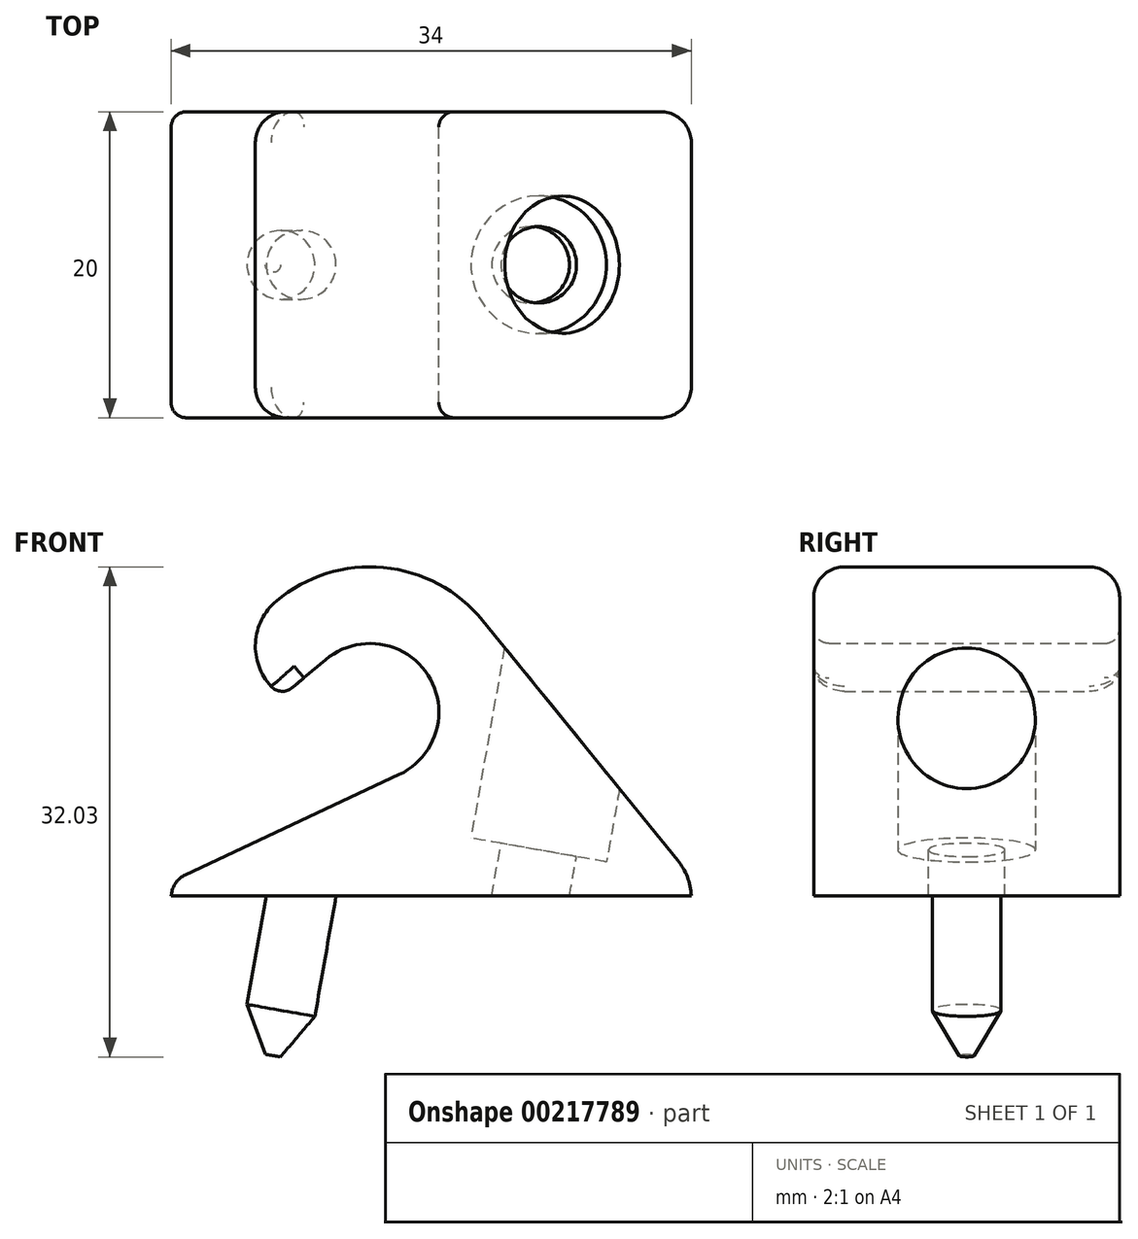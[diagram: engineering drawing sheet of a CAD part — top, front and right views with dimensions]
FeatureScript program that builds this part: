
annotation { "Feature Type Name" : "Feature", "Feature Type Description" : "" }
export const myFeature = defineFeature(function(context is Context, id is Id, definition is map)
    precondition{}
    {
        {
            var Q0;
            Q0=qCreatedBy(makeId("Front.planeOp"),FACE);
            var sketch = newSketch(context, id + "F0", { "sketchPlane" : qUnion([Q0])});
            skLineSegment(sketch, "E0", {"start": v(0, 0) * mm, "end": v(37, 0) * mm});
            skLineSegment(sketch, "E1", {"start": v(35.1, 2.33) * mm, "end": v(22.37, 18) * mm});
            skArc(sketch, "E2", {"start": v(16.9, 7.93) * mm, "mid": v(18.8, 14.43) * mm, "end": v(12.1, 15.44) * mm});
            skLineSegment(sketch, "E3", {"start": v(16.9, 7.93) * mm, "end": v(2.93, 1.37) * mm});
            skArc(sketch, "E4", {"start": v(22.37, 18) * mm, "mid": v(15.9, 21.46) * mm, "end": v(8.88, 19.27) * mm});
            skLineSegment(sketch, "E5", {"start": v(12.1, 15.44) * mm, "end": v(9.92, 13.6) * mm});
            skLineSegment(sketch, "E6", {"start": v(8.28, 14.37) * mm, "end": v(8.28, 14.37) * mm});
            skPoint(sketch, "E7.newPointB", {"position": v(8.28, 12.22) * mm});
            skArc(sketch, "E7.filletArc", {"start": v(8.28, 14.37) * mm, "mid": v(8.86, 13.46) * mm, "end": v(9.92, 13.6) * mm});
            skLineSegment(sketch, "E8", {"start": v(2, 0) * mm, "end": v(2.04, 0.2) * mm});
            skPoint(sketch, "E9.newPointB", {"position": v(0, 0) * mm});
            skArc(sketch, "E9.filletArc", {"start": v(2.93, 1.37) * mm, "mid": v(2.34, 0.9) * mm, "end": v(2.04, 0.2) * mm});
            skPoint(sketch, "E10.newPointA", {"position": v(37, 0) * mm});
            skArc(sketch, "E10.filletArc", {"start": v(36, 0) * mm, "mid": v(35.74, 1.23) * mm, "end": v(35.1, 2.33) * mm});
            skLineSegment(sketch, "E11", {"start": v(15, 12) * mm, "end": v(9.07, 19.04) * mm, "construction": true});
            skArc(sketch, "E12", {"start": v(8.88, 19.27) * mm, "mid": v(7.52, 16.55) * mm, "end": v(8.55, 13.69) * mm});
            skLineSegment(sketch, "E13", {"start": v(-3.54, 8.21) * mm, "end": v(45.39, -0.41) * mm, "construction": true});
            skPoint(sketch, "E14", {"position": v(26.03, 3) * mm});
            skLineSegment(sketch, "E15", {"start": v(26.03, 3) * mm, "end": v(24.94, -3.2) * mm, "construction": true});
            skPoint(sketch, "E16", {"position": v(25.5, 0) * mm});
            skLineSegment(sketch, "E17", {"start": v(11.48, 5.57) * mm, "end": v(10.5, 0) * mm, "construction": true});
            skLineSegment(sketch, "E18.0", {"start": v(-4.45, 3.04) * mm, "end": v(44.48, -5.59) * mm, "construction": true});
            skPoint(sketch, "E19", {"position": v(10.57, 0.4) * mm});
            skPoint(sketch, "E20", {"position": v(12.78, 0) * mm});
            skPoint(sketch, "E21.start.orphan", {"position": v(36, 0) * mm});
            skSolve(sketch);
        }
        {
            var Q0;
            Q0 = qSketchRegion(id + "F0", true);
            extrude(context, id + "F1", {"entities" : qUnion([Q0]), "endBound" : BoundingType.SYMMETRIC, "depth" : 20 * mm});
        }
        {
            var Q0;
            Q0=sQuery(id+"F0.wireOp",EDGE,"E13");
            cPlane(context, id + "F2", {"entities" : qUnion([Q0]), "cplaneType" : CPlaneType.LINE_ANGLE, "offset" : 25 * mm, "angle" : 90 * degree, "width" : 150 * mm, "height" : 150 * mm});
        }
        {
            var Q0;
            Q0=qCreatedBy(id+"F2.planeOp",FACE);
            var sketch = newSketch(context, id + "F3", { "sketchPlane" : qUnion([Q0])});
            skCircle(sketch, "E22", {"center": v(25.11, 0) * mm, "radius": 4.5 * mm});
            skSolve(sketch);
        }
        {
            var Q0;
            Q0 = qSketchRegion(id + "F3", true);
            extrude(context, id + "F4", {"entities" : qUnion([Q0]), "operationType" : NewBodyOperationType.REMOVE, "endBound" : BoundingType.THROUGH_ALL, "depth" : 25 * mm});
        }
        {
            var Q0;
            Q0=qCreatedBy(id+"F2.planeOp",FACE);
            var sketch = newSketch(context, id + "F5", { "sketchPlane" : qUnion([Q0])});
            skCircle(sketch, "E23", {"center": v(25.11, 0) * mm, "radius": 2.5 * mm});
            skSolve(sketch);
        }
        {
            var Q0;
            Q0 = qSketchRegion(id + "F5", true);
            extrude(context, id + "F6", {"entities" : qUnion([Q0]), "operationType" : NewBodyOperationType.REMOVE, "endBound" : BoundingType.THROUGH_ALL, "oppositeDirection" : true, "depth" : 25 * mm});
        }
        {
            var Q0;
            Q0=sQuery(id+"F0.wireOp",EDGE,"E18.0");
            cPlane(context, id + "F7", {"entities" : qUnion([Q0]), "cplaneType" : CPlaneType.LINE_ANGLE, "offset" : 25 * mm, "angle" : 90 * degree, "width" : 150 * mm, "height" : 150 * mm});
        }
        {
            var Q0;
            Q0=qCreatedBy(id+"F7.planeOp",FACE);
            var sketch = newSketch(context, id + "F8", { "sketchPlane" : qUnion([Q0])});
            skCircle(sketch, "E24", {"center": v(10.34, 0) * mm, "radius": 2.25 * mm});
            skSolve(sketch);
        }
        {
            var Q0;
            Q0 = qSketchRegion(id + "F8", true);
            extrude(context, id + "F9", {"entities" : qUnion([Q0]), "operationType" : NewBodyOperationType.ADD, "oppositeDirection" : true, "depth" : 8 * mm});
        }
        {
            var Q0;
            Q0=makeQuery(id+"F9.opExtrude","CAP_FACE",FACE,{"disambiguationData":[OSD([sQuery(id+"F8.wireOp",EDGE,"E24")])],"isStart":false});
            cPlane(context, id + "F10", {"entities" : qUnion([Q0]), "cplaneType" : CPlaneType.OFFSET, "offset" : 3 * mm, "width" : 150 * mm, "height" : 150 * mm});
        }
        {
            var Q0;
            Q0=qCreatedBy(id+"F10.planeOp",FACE);
            var sketch = newSketch(context, id + "F11", { "sketchPlane" : qUnion([Q0])});
            skCircle(sketch, "E25", {"center": v(10.34, 0) * mm, "radius": 0.5 * mm});
            skSolve(sketch);
        }
        {
            var Q1;
            Q1=makeQuery(id+"F9.opExtrude","CAP_FACE",FACE,{"disambiguationData":[OSD([sQuery(id+"F8.wireOp",EDGE,"E24")])],"isStart":false});
            var Q2;
            Q2=makeQuery(id+"F11.imprint","IMPRINT",FACE,{"disambiguationData":[TD([[makeQuery(id+"F11.imprint","IMPRINT",EDGE,{"derivedFrom":sQuery(id+"F11.wireOp",EDGE,"E25")}),1.0]])]});
            loft(context, id + "F12", {"operationType" : NewBodyOperationType.ADD, "sheetProfilesArray" : [{ "sheetProfileEntities" : qUnion([Q1]) }, { "sheetProfileEntities" : qUnion([Q2]) }]});
        }
        {
            var Q0;
            {var subQ0=sQuery(id+"F0.wireOp",EDGE,"E10.filletArc");Q0=makeQuery(id+"F1.opExtrude","CAP_EDGE",EDGE,{"disambiguationData":[OSD([subQ0]),TDD([makeQuery(id+"F0.imprint","IMPRINT",EDGE,{"disambiguationData":[TD([[makeQuery(id+"F0.imprint","INTERSECT",VERTEX,{"derivedFrom":[sQuery(id+"F0.wireOp",EDGE,"E1"),subQ0]}),1.0]])],"derivedFrom":subQ0})])],"isStart":false});}
            var Q1;
            Q1=makeQuery(id+"F1.opExtrude","CAP_EDGE",EDGE,{"disambiguationData":[OSD([sQuery(id+"F0.wireOp",EDGE,"E1")])],"isStart":false});
            var Q2;
            Q2=makeQuery(id+"F1.opExtrude","CAP_EDGE",EDGE,{"disambiguationData":[OSD([sQuery(id+"F0.wireOp",EDGE,"E4")])],"isStart":false});
            var Q3;
            Q3=makeQuery(id+"F1.opExtrude","CAP_EDGE",EDGE,{"disambiguationData":[OSD([sQuery(id+"F0.wireOp",EDGE,"E12")])],"isStart":false});
            var Q4;
            {var subQ0=sQuery(id+"F0.wireOp",EDGE,"E10.filletArc");Q4=makeQuery(id+"F1.opExtrude","CAP_EDGE",EDGE,{"disambiguationData":[OSD([subQ0]),TDD([makeQuery(id+"F0.imprint","IMPRINT",EDGE,{"disambiguationData":[TD([[makeQuery(id+"F0.imprint","INTERSECT",VERTEX,{"derivedFrom":[sQuery(id+"F0.wireOp",EDGE,"E1"),subQ0]}),1.0]])],"derivedFrom":subQ0})])],"isStart":true});}
            var Q5;
            Q5=makeQuery(id+"F1.opExtrude","CAP_EDGE",EDGE,{"disambiguationData":[OSD([sQuery(id+"F0.wireOp",EDGE,"E1")])],"isStart":true});
            var Q6;
            Q6=makeQuery(id+"F1.opExtrude","CAP_EDGE",EDGE,{"disambiguationData":[OSD([sQuery(id+"F0.wireOp",EDGE,"E4")])],"isStart":true});
            var Q7;
            Q7=makeQuery(id+"F1.opExtrude","CAP_EDGE",EDGE,{"disambiguationData":[OSD([sQuery(id+"F0.wireOp",EDGE,"E12")])],"isStart":true});
            fillet(context, id + "F13", {"entities" : qUnion([Q0, Q1, Q2, Q3, Q4, Q5, Q6, Q7]), "radius" : 2 * mm, "allowEdgeOverflow" : false});
        }
        {
            var Q0;
            Q0=makeQuery(id+"F1.opExtrude","CAP_EDGE",EDGE,{"disambiguationData":[OSD([sQuery(id+"F0.wireOp",EDGE,"E2")])],"isStart":false});
            var Q1;
            Q1=makeQuery(id+"F1.opExtrude","CAP_EDGE",EDGE,{"disambiguationData":[OSD([sQuery(id+"F0.wireOp",EDGE,"E5")])],"isStart":false});
            var Q2;
            Q2=makeQuery(id+"F13.opFillet","BLEND_EDGE",EDGE,{"blendedFrom":[makeQuery(id+"F1.opExtrude","CAP_EDGE",EDGE,{"disambiguationData":[OSD([sQuery(id+"F0.wireOp",EDGE,"E12")])],"isStart":false}),makeQuery(id+"F1.opExtrude","SWEPT_FACE",FACE,{"disambiguationData":[OSD([sQuery(id+"F0.wireOp",EDGE,"E5")])]})],"blendedInto":[makeQuery(id+"F1.opExtrude","SWEPT_FACE",FACE,{"disambiguationData":[OSD([sQuery(id+"F0.wireOp",EDGE,"E5")])]})]});
            var Q3;
            Q3=makeQuery(id+"F13.opFillet","BLEND_EDGE",EDGE,{"blendedFrom":[makeQuery(id+"F1.opExtrude","CAP_EDGE",EDGE,{"disambiguationData":[OSD([sQuery(id+"F0.wireOp",EDGE,"E12")])],"isStart":false}),makeQuery(id+"F1.opExtrude","SWEPT_FACE",FACE,{"disambiguationData":[OSD([sQuery(id+"F0.wireOp",EDGE,"E7.filletArc")])]})],"blendedInto":[makeQuery(id+"F1.opExtrude","SWEPT_FACE",FACE,{"disambiguationData":[OSD([sQuery(id+"F0.wireOp",EDGE,"E7.filletArc")])]})]});
            var Q4;
            Q4=makeQuery(id+"F1.opExtrude","CAP_EDGE",EDGE,{"disambiguationData":[OSD([sQuery(id+"F0.wireOp",EDGE,"E9.filletArc")])],"isStart":true});
            var Q5;
            Q5=makeQuery(id+"F1.opExtrude","CAP_EDGE",EDGE,{"disambiguationData":[OSD([sQuery(id+"F0.wireOp",EDGE,"E8")])],"isStart":true});
            var Q6;
            Q6=makeQuery(id+"F1.opExtrude","CAP_EDGE",EDGE,{"disambiguationData":[OSD([sQuery(id+"F0.wireOp",EDGE,"E3")])],"isStart":true});
            var Q7;
            Q7=makeQuery(id+"F1.opExtrude","CAP_EDGE",EDGE,{"disambiguationData":[OSD([sQuery(id+"F0.wireOp",EDGE,"E2")])],"isStart":true});
            var Q8;
            Q8=makeQuery(id+"F1.opExtrude","CAP_EDGE",EDGE,{"disambiguationData":[OSD([sQuery(id+"F0.wireOp",EDGE,"E5")])],"isStart":true});
            var Q9;
            Q9=makeQuery(id+"F13.opFillet","BLEND_EDGE",EDGE,{"blendedFrom":[makeQuery(id+"F1.opExtrude","CAP_EDGE",EDGE,{"disambiguationData":[OSD([sQuery(id+"F0.wireOp",EDGE,"E12")])],"isStart":true}),makeQuery(id+"F1.opExtrude","SWEPT_FACE",FACE,{"disambiguationData":[OSD([sQuery(id+"F0.wireOp",EDGE,"E5")])]})],"blendedInto":[makeQuery(id+"F1.opExtrude","SWEPT_FACE",FACE,{"disambiguationData":[OSD([sQuery(id+"F0.wireOp",EDGE,"E5")])]})]});
            var Q10;
            Q10=makeQuery(id+"F13.opFillet","BLEND_EDGE",EDGE,{"blendedFrom":[makeQuery(id+"F1.opExtrude","CAP_EDGE",EDGE,{"disambiguationData":[OSD([sQuery(id+"F0.wireOp",EDGE,"E12")])],"isStart":true}),makeQuery(id+"F1.opExtrude","SWEPT_FACE",FACE,{"disambiguationData":[OSD([sQuery(id+"F0.wireOp",EDGE,"E7.filletArc")])]})],"blendedInto":[makeQuery(id+"F1.opExtrude","SWEPT_FACE",FACE,{"disambiguationData":[OSD([sQuery(id+"F0.wireOp",EDGE,"E7.filletArc")])]})]});
            fillet(context, id + "F14", {"entities" : qUnion([Q0, Q1, Q2, Q3, Q4, Q5, Q6, Q7, Q8, Q9, Q10]), "radius" : 1 * mm, "tangentPropagation" : true, "allowEdgeOverflow" : false});
        }
    });
